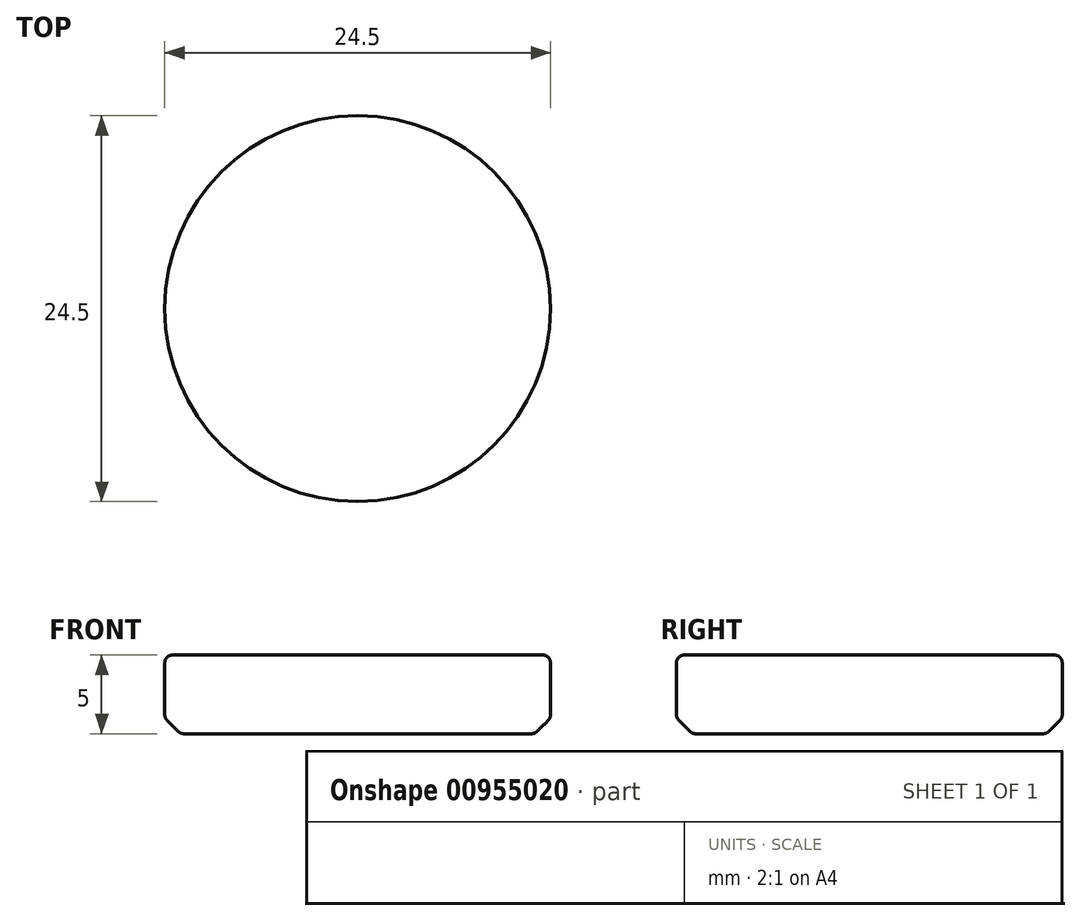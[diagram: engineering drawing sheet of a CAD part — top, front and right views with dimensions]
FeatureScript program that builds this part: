
annotation { "Feature Type Name" : "Feature", "Feature Type Description" : "" }
export const myFeature = defineFeature(function(context is Context, id is Id, definition is map)
    precondition{}
    {
        {
            var Q0;
            Q0=qCreatedBy(makeId("Top.planeOp"),FACE);
            var sketch = newSketch(context, id + "F0", { "sketchPlane" : qUnion([Q0])});
            skCircle(sketch, "E0", {"center": v(0, 0) * mm, "radius": 12.25 * mm});
            skSolve(sketch);
        }
        {
            var Q0;
            Q0 = qSketchRegion(id + "F0", true);
            extrude(context, id + "F1", {"entities" : qUnion([Q0]), "depth" : 5 * mm, "offsetDistance" : 25.4 * mm});
        }
        {
            var Q0;
            Q0=makeQuery(id+"F1.opExtrude","CAP_EDGE",EDGE,{"disambiguationData":[OSD([sQuery(id+"F0.wireOp",EDGE,"E0")])],"isStart":true});
            chamfer(context, id + "F2", {"entities" : qUnion([Q0]), "width" : 1 * mm, "tangentPropagation" : true});
        }
        {
            var Q0;
            Q0=makeQuery(id+"F1.opExtrude","CAP_EDGE",EDGE,{"disambiguationData":[OSD([sQuery(id+"F0.wireOp",EDGE,"E0")])],"isStart":false});
            var Q1;
            {var subQ0=sQuery(id+"F0.wireOp",EDGE,"E0");Q1=makeQuery(id+"F2.opChamfer","BLEND_EDGE",EDGE,{"blendedFrom":[makeQuery(id+"F1.opExtrude","CAP_EDGE",EDGE,{"disambiguationData":[OSD([subQ0])],"isStart":true}),makeQuery(id+"F1.opExtrude","SWEPT_FACE",FACE,{"disambiguationData":[OSD([subQ0])]})],"blendedInto":[makeQuery(id+"F1.opExtrude","SWEPT_FACE",FACE,{"disambiguationData":[OSD([subQ0])]})]});}
            var Q2;
            {var subQ0=sQuery(id+"F0.wireOp",EDGE,"E0");Q2=makeQuery(id+"F2.opChamfer","BLEND_EDGE",EDGE,{"blendedFrom":[makeQuery(id+"F1.opExtrude","CAP_EDGE",EDGE,{"disambiguationData":[OSD([subQ0])],"isStart":true}),makeQuery(id+"F1.opExtrude","CAP_FACE",FACE,{"disambiguationData":[OSD([subQ0])],"isStart":true})],"blendedInto":[makeQuery(id+"F1.opExtrude","CAP_FACE",FACE,{"disambiguationData":[OSD([subQ0])],"isStart":true})]});}
            fillet(context, id + "F3", {"entities" : qUnion([Q0, Q1, Q2]), "radius" : .5 * mm, "tangentPropagation" : true, "allowEdgeOverflow" : false});
        }
    });
